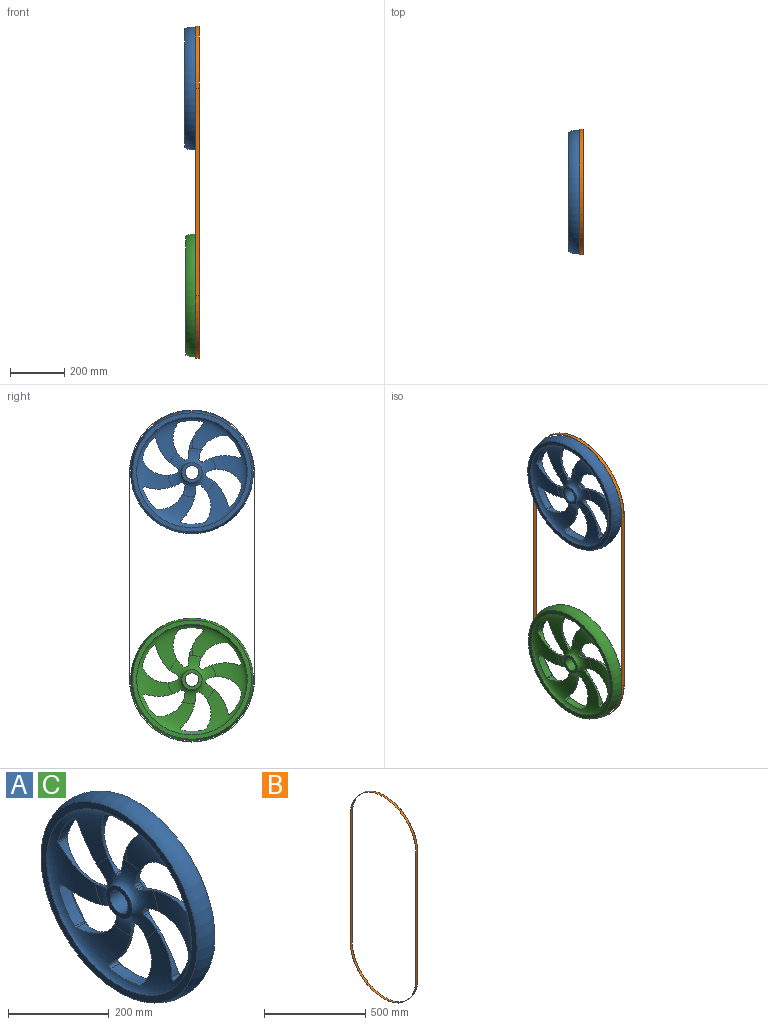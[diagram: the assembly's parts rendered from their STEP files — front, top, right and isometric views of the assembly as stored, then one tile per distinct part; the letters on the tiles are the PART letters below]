
ASSEMBLY  parts=3 mates=3
PART A: 60 faces, bbox 60.5x488.8x488.8 mm
  f0: revolved ~406.4x406.4mm, area 63111.9mm2, adj f1,f5,f6,f12,f13,f14,f17,f18
  f1: revolved ~33x14.08mm, area 187.5mm2, adj f0,f5,f42
  f2: revolved ~406.4x406.4mm, area 63111.9mm2, adj f3,f4,f8,f12,f13,f14,f17,f18
  f3: revolved ~33x14.08mm, area 187.5mm2, adj f2,f4,f42
  f4: revolved ~177x177mm, area 38711.9mm2, adj f2,f3,f9,f15,f16,f17,f18,f19
  f5: revolved ~177x177mm, area 38711.9mm2, adj f0,f1,f11,f15,f16,f17,f18,f19
  f6: plane 438.15x438.15mm, normal (1,0,0), area 21060mm2, adj f0,f7
  f7: torus R=175.77mm, axis (-1,0,0), area 73535.2mm2, adj f6,f8
  f8: plane 438.15x438.15mm, normal (-1,0,0), area 21060mm2, adj f2,f7
  f9: plane 74x74mm, normal (-1,0,0), area 2337.3mm2, adj f4,f10
  f10: cylinder r=25mm len=50mm, axis (-1,0,0), area 7854mm2, adj f9,f11
  f11: plane 74x74mm, normal (1,0,0), area 2337.3mm2, adj f5,f10
  f12: cylinder r=6mm len=26.98mm, axis (-1,0,0), area 106.5mm2, adj f0,f2,f13,f17
  f13: cylinder r=190.5mm len=74.45mm, axis (-1,0,0), area 2303.7mm2, adj f0,f2,f12,f14
  f14: cylinder r=6mm len=26.98mm, axis (-1,0,0), area 317.3mm2, adj f0,f2,f13,f18
  f15: cylinder r=50.8mm len=16.51mm, axis (-1,0,0), area 92.7mm2, adj f4,f5,f16,f19
  f16: cylinder r=6mm len=16.51mm, axis (-1,0,0), area 99.5mm2, adj f4,f5,f15,f17
  f17: cylinder r=95.54mm len=129.12mm, axis (-1,0,0), area 1564.4mm2, adj f0,f2,f4,f5,f12,f16
  f18: cylinder r=160.35mm len=107.77mm, axis (-1,0,0), area 1206.8mm2, adj f0,f2,f4,f5,f14,f19
  f19: cylinder r=6mm len=16.51mm, axis (-1,0,0), area 114.9mm2, adj f4,f5,f15,f18
  f20: cylinder r=6mm len=26.98mm, axis (-1,0,0), area 106.5mm2, adj f0,f2,f21,f25
  f21: cylinder r=190.5mm len=72.18mm, axis (-1,0,0), area 2303.7mm2, adj f0,f2,f20,f22
  f22: cylinder r=6mm len=26.98mm, axis (-1,0,0), area 317.3mm2, adj f0,f2,f21,f26
  f23: cylinder r=50.8mm len=16.51mm, axis (-1,0,0), area 92.7mm2, adj f4,f5,f24,f27
  f24: cylinder r=6mm len=16.51mm, axis (-1,0,0), area 99.5mm2, adj f4,f5,f23,f25
  f25: cylinder r=95.54mm len=107mm, axis (-1,0,0), area 1564.4mm2, adj f0,f2,f4,f5,f20,f24
  f26: cylinder r=160.35mm len=133.18mm, axis (-1,0,0), area 1206.8mm2, adj f0,f2,f4,f5,f22,f27
  f27: cylinder r=6mm len=16.51mm, axis (-1,0,0), area 114.9mm2, adj f4,f5,f23,f26
  f28: cylinder r=6mm len=26.98mm, axis (-1,0,0), area 106.5mm2, adj f0,f2,f29,f33
  f29: cylinder r=190.5mm len=74.45mm, axis (-1,0,0), area 2303.7mm2, adj f0,f2,f28,f30
  f30: cylinder r=6mm len=26.98mm, axis (-1,0,0), area 317.3mm2, adj f0,f2,f29,f34
  f31: cylinder r=50.8mm len=16.51mm, axis (-1,0,0), area 92.7mm2, adj f4,f5,f32,f35
  f32: cylinder r=6mm len=16.51mm, axis (-1,0,0), area 99.5mm2, adj f4,f5,f31,f33
  f33: cylinder r=95.54mm len=129.12mm, axis (-1,0,0), area 1564.4mm2, adj f0,f2,f4,f5,f28,f32
  f34: cylinder r=160.35mm len=107.77mm, axis (-1,0,0), area 1206.8mm2, adj f0,f2,f4,f5,f30,f35
  f35: cylinder r=6mm len=16.51mm, axis (-1,0,0), area 114.9mm2, adj f4,f5,f31,f34
  f36: cylinder r=6mm len=26.98mm, axis (-1,0,0), area 106.5mm2, adj f0,f2,f37,f41
  f37: cylinder r=190.5mm len=84.66mm, axis (-1,0,0), area 2303.7mm2, adj f0,f2,f36,f38
  f38: cylinder r=6mm len=26.98mm, axis (-1,0,0), area 317.3mm2, adj f0,f2,f37,f42
  f39: cylinder r=50.8mm len=16.51mm, axis (-1,0,0), area 92.7mm2, adj f4,f5,f40,f43
  f40: cylinder r=6mm len=16.51mm, axis (-1,0,0), area 99.5mm2, adj f4,f5,f39,f41
  f41: cylinder r=95.54mm len=136.32mm, axis (-1,0,0), area 1564.4mm2, adj f0,f2,f4,f5,f36,f40
  f42: cylinder r=160.35mm len=122.9mm, axis (-1,0,0), area 1215.8mm2, adj f0,f1,f2,f3,f4,f5,f38,f43
  f43: cylinder r=6mm len=16.51mm, axis (-1,0,0), area 114.9mm2, adj f4,f5,f39,f42
  f44: cylinder r=6mm len=26.98mm, axis (-1,0,0), area 106.5mm2, adj f0,f2,f45,f49
  f45: cylinder r=190.5mm len=84.66mm, axis (-1,0,0), area 2303.7mm2, adj f0,f2,f44,f46
  f46: cylinder r=6mm len=26.98mm, axis (-1,0,0), area 317.3mm2, adj f0,f2,f45,f50
  f47: cylinder r=50.8mm len=16.51mm, axis (-1,0,0), area 92.7mm2, adj f4,f5,f48,f51
  f48: cylinder r=6mm len=16.51mm, axis (-1,0,0), area 99.5mm2, adj f4,f5,f47,f49
  f49: cylinder r=95.54mm len=136.32mm, axis (-1,0,0), area 1564.4mm2, adj f0,f2,f4,f5,f44,f48
  f50: cylinder r=160.35mm len=122.9mm, axis (-1,0,0), area 1206.8mm2, adj f0,f2,f4,f5,f46,f51
  f51: cylinder r=6mm len=16.51mm, axis (-1,0,0), area 114.9mm2, adj f4,f5,f47,f50
  f52: cylinder r=6mm len=26.98mm, axis (-1,0,0), area 106.5mm2, adj f0,f2,f53,f57
  f53: cylinder r=190.5mm len=72.18mm, axis (-1,0,0), area 2303.7mm2, adj f0,f2,f52,f54
  f54: cylinder r=6mm len=26.98mm, axis (-1,0,0), area 317.3mm2, adj f0,f2,f53,f58
  f55: cylinder r=50.8mm len=16.51mm, axis (-1,0,0), area 92.7mm2, adj f4,f5,f56,f59
  f56: cylinder r=6mm len=16.51mm, axis (-1,0,0), area 99.5mm2, adj f4,f5,f55,f57
  f57: cylinder r=95.54mm len=107mm, axis (-1,0,0), area 1564.4mm2, adj f0,f2,f4,f5,f52,f56
  f58: cylinder r=160.35mm len=133.18mm, axis (-1,0,0), area 1206.8mm2, adj f0,f2,f4,f5,f54,f59
  f59: cylinder r=6mm len=16.51mm, axis (-1,0,0), area 114.9mm2, adj f4,f5,f55,f58
PART B: 10 faces, bbox 12.7x459x1221 mm
  f0: plane 762x12.7mm, normal (0,-1,0), area 9677.4mm2, adj f1,f7,f8,f9
  f1: cylinder r=229.49mm len=458.98mm, axis (-1,0,0), area 9156.2mm2, adj f0,f2,f8,f9
  f2: plane 762x12.7mm, normal (0,1,0), area 9677.4mm2, adj f1,f7,f8,f9
  f3: plane 762x12.7mm, normal (0,1,0), area 9677.4mm2, adj f4,f6,f8,f9
  f4: cylinder r=228.6mm len=457.2mm, axis (-1,0,0), area 9120.7mm2, adj f3,f5,f8,f9
  f5: plane 762x12.7mm, normal (0,-1,0), area 9677.4mm2, adj f4,f6,f8,f9
  f6: cylinder r=228.6mm len=457.2mm, axis (-1,0,0), area 9120.7mm2, adj f3,f5,f8,f9
  f7: cylinder r=229.49mm len=458.98mm, axis (-1,0,0), area 9156.2mm2, adj f0,f2,f8,f9
  f8: plane 1220.98x458.98mm, normal (1,0,0), area 2634.2mm2, adj f0,f1,f2,f3,f4,f5,f6,f7
  f9: plane 1220.98x458.98mm, normal (-1,0,0), area 2634.2mm2, adj f0,f1,f2,f3,f4,f5,f6,f7
PART C: same geometry as A
PLACE A at identity
PLACE B t=(21.83,0,0)mm
PLACE C t=(3.18,0,-762)mm
MATE planar A.f7 <-> C.f7  axis (-1,0,0) through (3.18,0,0)mm
MATE cylindrical B.f1 <-> C.f7  axis (1,0,0) through (28.18,0,-762)mm
MATE cylindrical B.f7 <-> A.f7  axis (-1,0,0) through (15.48,0,0)mm
